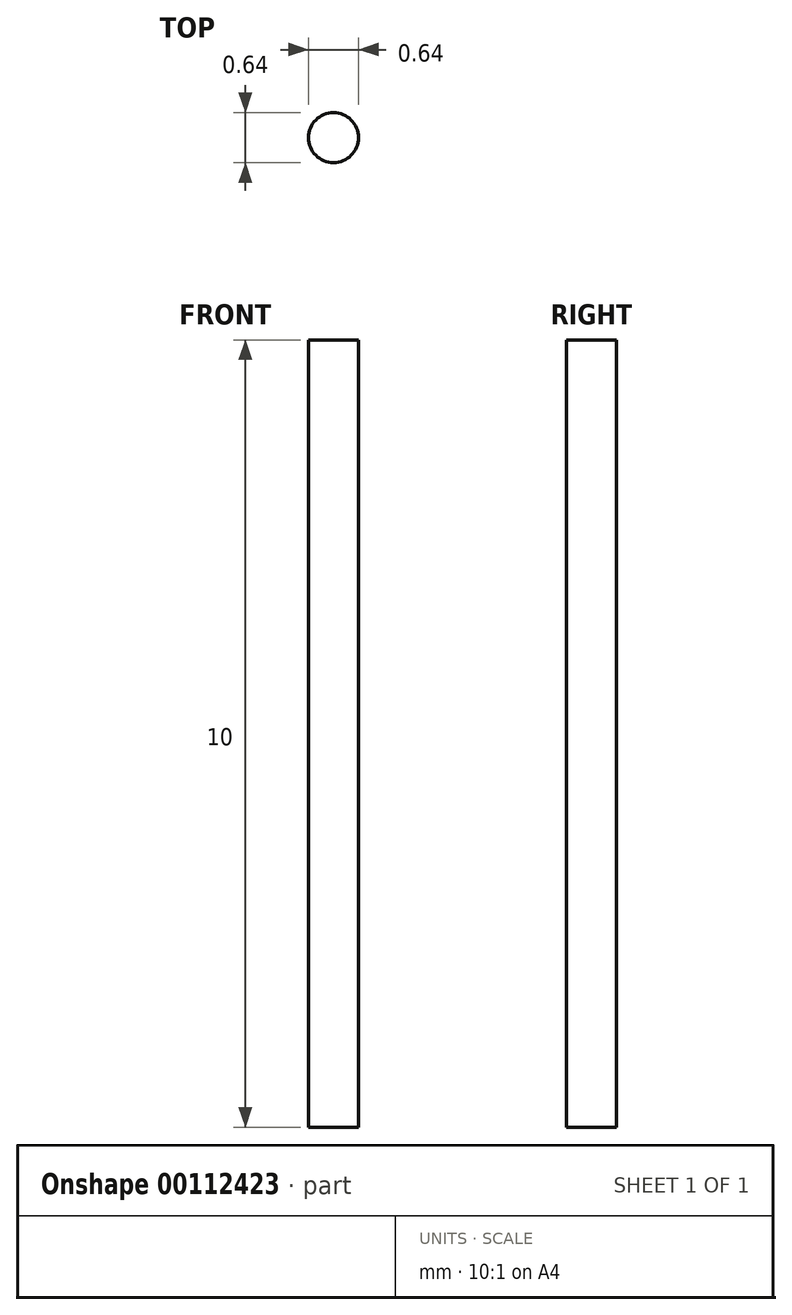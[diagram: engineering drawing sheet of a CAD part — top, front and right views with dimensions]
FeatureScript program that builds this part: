
annotation { "Feature Type Name" : "Feature", "Feature Type Description" : "" }
export const myFeature = defineFeature(function(context is Context, id is Id, definition is map)
    precondition{}
    {
        {
            var Q0;
            Q0=qCreatedBy(makeId("Top.planeOp"),FACE);
            var sketch = newSketch(context, id + "F0", { "sketchPlane" : qUnion([Q0])});
            skCircle(sketch, "E0", {"center": v(0, 0) * mm, "radius": 0.32 * mm});
            skSolve(sketch);
        }
        {
            var Q0;
            Q0=qSketchRegion(id+"F0",true);
            extrude(context, id + "F1", {"entities" : qUnion([Q0]), "depth" : 10 * mm});
        }
    });
